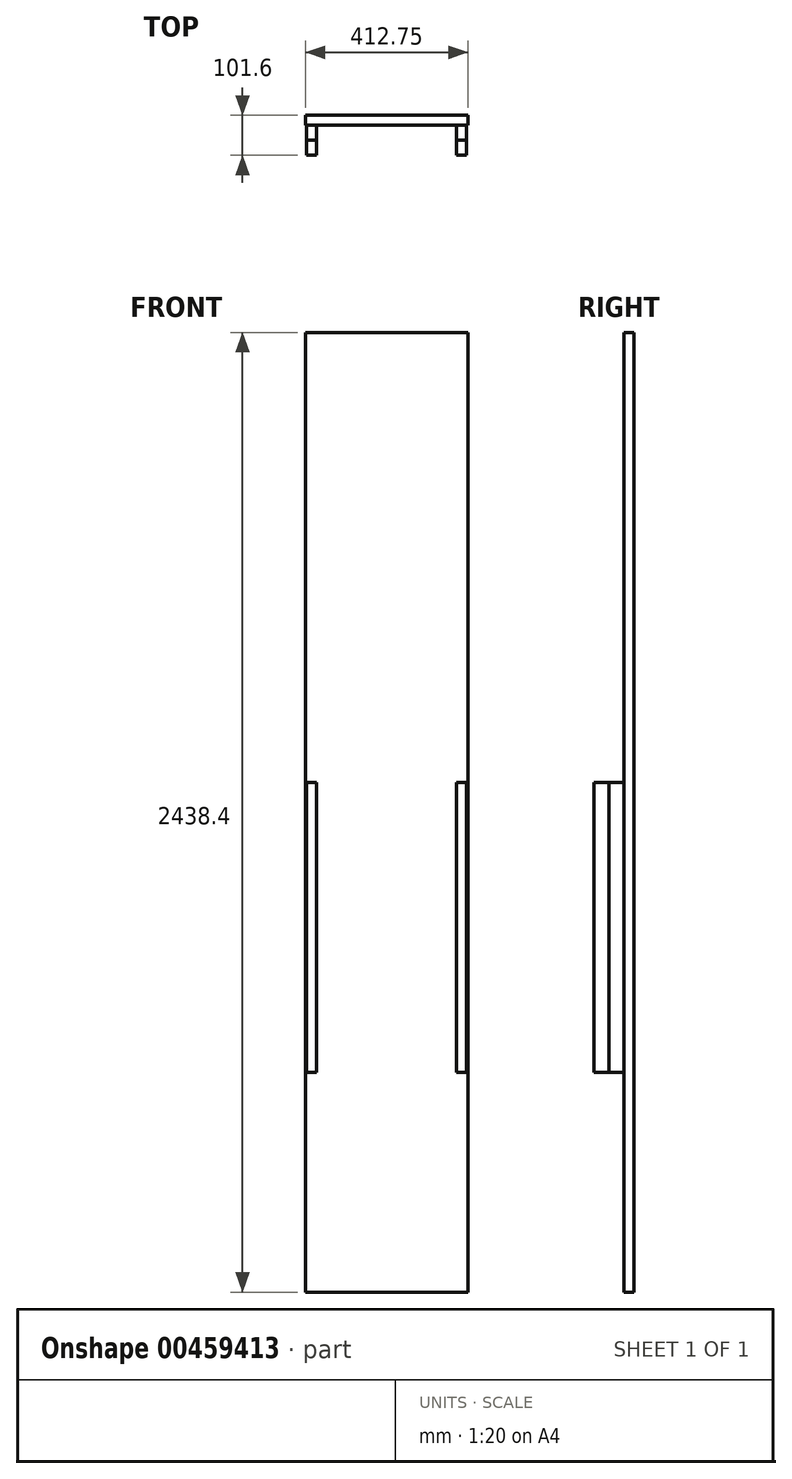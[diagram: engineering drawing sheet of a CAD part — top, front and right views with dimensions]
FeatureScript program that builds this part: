
annotation { "Feature Type Name" : "Feature", "Feature Type Description" : "" }
export const myFeature = defineFeature(function(context is Context, id is Id, definition is map)
    precondition{}
    {
        {
            var Q0;
            Q0=qCreatedBy(makeId("Front.planeOp"),FACE);
            var sketch = newSketch(context, id + "F0", { "sketchPlane" : qUnion([Q0])});
            skLineSegment(sketch, "E0.bottom", {"start": v(0, 0) * mm, "end": v(412.75, 0) * mm});
            skLineSegment(sketch, "E0.top", {"start": v(0, 2438.4) * mm, "end": v(412.75, 2438.4) * mm});
            skLineSegment(sketch, "E0.left", {"start": v(0, 0) * mm, "end": v(0, 2438.4) * mm});
            skLineSegment(sketch, "E0.right", {"start": v(412.75, 0) * mm, "end": v(412.75, 2438.4) * mm});
            skSolve(sketch);
        }
        {
            var Q0;
            Q0 = qSketchRegion(id + "F0", true);
            extrude(context, id + "F1", {"entities" : qUnion([Q0]), "depth" : 25.4 * mm});
        }
        {
            var Q0;
            Q0=makeQuery(id+"F1.opExtrude","CAP_FACE",FACE,{"disambiguationData":[OSD([sQuery(id+"F0.wireOp",EDGE,"E0.bottom"),sQuery(id+"F0.wireOp",EDGE,"E0.top"),sQuery(id+"F0.wireOp",EDGE,"E0.left"),sQuery(id+"F0.wireOp",EDGE,"E0.right")])],"isStart":false});
            var sketch = newSketch(context, id + "F2", { "sketchPlane" : qUnion([Q0])});
            skLineSegment(sketch, "E1.bottom", {"start": v(3.17, 863.6) * mm, "end": v(409.58, 863.6) * mm});
            skLineSegment(sketch, "E1.top", {"start": v(3.18, 127) * mm, "end": v(409.57, 127) * mm, "construction": true});
            skLineSegment(sketch, "E1.left", {"start": v(3.18, 863.6) * mm, "end": v(3.17, 127) * mm});
            skLineSegment(sketch, "E1.right", {"start": v(409.58, 863.6) * mm, "end": v(409.58, 127) * mm});
            skLineSegment(sketch, "E2", {"start": v(206.38, 127) * mm, "end": v(206.38, 0) * mm, "construction": true});
            skLineSegment(sketch, "E3", {"start": v(3.18, 127) * mm, "end": v(28.58, 127) * mm});
            skLineSegment(sketch, "E4", {"start": v(28.58, 127) * mm, "end": v(28.58, 800.1) * mm});
            skLineSegment(sketch, "E5", {"start": v(28.58, 800.1) * mm, "end": v(384.18, 800.1) * mm});
            skLineSegment(sketch, "E6", {"start": v(384.18, 800.1) * mm, "end": v(384.18, 127) * mm});
            skLineSegment(sketch, "E7", {"start": v(384.18, 127) * mm, "end": v(409.58, 127) * mm});
            skSolve(sketch);
        }
        {
            var Q0;
            Q0 = qSketchRegion(id + "F2", true);
            extrude(context, id + "F3", {"entities" : qUnion([Q0]), "depth" : 76.2 * mm});
        }
        {
            var Q0;
            Q0=makeQuery(id+"F1.opExtrude","CAP_FACE",FACE,{"disambiguationData":[OSD([sQuery(id+"F0.wireOp",EDGE,"E0.bottom"),sQuery(id+"F0.wireOp",EDGE,"E0.top"),sQuery(id+"F0.wireOp",EDGE,"E0.left"),sQuery(id+"F0.wireOp",EDGE,"E0.right")])],"isStart":false});
            var sketch = newSketch(context, id + "F4", { "sketchPlane" : qUnion([Q0])});
            skLineSegment(sketch, "E8.bottom", {"start": v(3.18, 711.2) * mm, "end": v(409.57, 711.2) * mm});
            skLineSegment(sketch, "E8.top", {"start": v(3.17, 1295.4) * mm, "end": v(409.58, 1295.4) * mm});
            skLineSegment(sketch, "E8.left", {"start": v(3.17, 711.2) * mm, "end": v(3.17, 1295.4) * mm});
            skLineSegment(sketch, "E8.right", {"start": v(409.58, 711.2) * mm, "end": v(409.57, 1295.4) * mm});
            skLineSegment(sketch, "E9", {"start": v(206.37, 711.2) * mm, "end": v(206.38, 0) * mm, "construction": true});
            skSolve(sketch);
        }
        {
            var Q0;
            Q0 = qSketchRegion(id + "F4", true);
            extrude(context, id + "F5", {"entities" : qUnion([Q0]), "depth" : 38.1 * mm});
        }
        {
            var Q0;
            Q0=makeQuery(id+"F5.opExtrude","CAP_FACE",FACE,{"disambiguationData":[OSD([sQuery(id+"F4.wireOp",EDGE,"E8.bottom"),sQuery(id+"F4.wireOp",EDGE,"E8.top"),sQuery(id+"F4.wireOp",EDGE,"E8.left"),sQuery(id+"F4.wireOp",EDGE,"E8.right")])],"isStart":false});
            var sketch = newSketch(context, id + "F6", { "sketchPlane" : qUnion([Q0])});
            skLineSegment(sketch, "E10", {"start": v(152.7, 1295.4) * mm, "end": v(148.35, 717.4) * mm});
            skSolve(sketch);
        }
        {
            var Q0;
            Q0=makeQuery(id+"F6.imprint","IMPRINT",FACE,{"disambiguationData":[TD([[makeQuery(id+"F6.imprint","IMPRINT",EDGE,{"derivedFrom":makeQuery(id+"F5.opExtrude","CAP_EDGE",EDGE,{"disambiguationData":[OSD([sQuery(id+"F4.wireOp",EDGE,"E8.bottom")])],"isStart":false})}),1.0]])]});
            var sketch = newSketch(context, id + "F7", { "sketchPlane" : qUnion([Q0])});
            skLineSegment(sketch, "E11.bottom", {"start": v(28.57, 1295.4) * mm, "end": v(3.17, 1295.4) * mm});
            skLineSegment(sketch, "E11.top", {"start": v(28.58, 558.8) * mm, "end": v(3.18, 558.8) * mm});
            skLineSegment(sketch, "E11.left", {"start": v(28.57, 1295.4) * mm, "end": v(28.58, 558.8) * mm});
            skLineSegment(sketch, "E11.right", {"start": v(3.17, 1295.4) * mm, "end": v(3.18, 558.8) * mm});
            skLineSegment(sketch, "E12.bottom", {"start": v(409.58, 558.8) * mm, "end": v(384.18, 558.8) * mm});
            skLineSegment(sketch, "E12.top", {"start": v(409.57, 1295.4) * mm, "end": v(384.17, 1295.4) * mm});
            skLineSegment(sketch, "E12.left", {"start": v(409.58, 558.8) * mm, "end": v(409.57, 1295.4) * mm});
            skLineSegment(sketch, "E12.right", {"start": v(384.18, 558.8) * mm, "end": v(384.17, 1295.4) * mm});
            skSolve(sketch);
        }
        {
            var Q0;
            Q0 = qSketchRegion(id + "F7", true);
            extrude(context, id + "F8", {"entities" : qUnion([Q0]), "depth" : 38.1 * mm});
        }
        {
            var Q0;
            Q0=makeQuery(id+"F8.opExtrude","CAP_FACE",FACE,{"disambiguationData":[OSD([sQuery(id+"F7.wireOp",EDGE,"E11.bottom"),sQuery(id+"F7.wireOp",EDGE,"E11.top"),sQuery(id+"F7.wireOp",EDGE,"E11.left"),sQuery(id+"F7.wireOp",EDGE,"E11.right")])],"isStart":true});
            var sketch = newSketch(context, id + "F9", { "sketchPlane" : qUnion([Q0])});
            skLineSegment(sketch, "E13.0.0", {"start": v(-28.58, 558.8) * mm, "end": v(-28.57, 1295.4) * mm});
            skLineSegment(sketch, "E13.0.1", {"start": v(-28.57, 1295.4) * mm, "end": v(-3.17, 1295.4) * mm});
            skLineSegment(sketch, "E13.0.2", {"start": v(-3.17, 1295.4) * mm, "end": v(-3.18, 558.8) * mm});
            skLineSegment(sketch, "E13.0.3", {"start": v(-3.18, 558.8) * mm, "end": v(-28.58, 558.8) * mm});
            skLineSegment(sketch, "E13.1.0", {"start": v(-384.17, 1295.4) * mm, "end": v(-384.18, 558.8) * mm});
            skLineSegment(sketch, "E13.1.1", {"start": v(-384.18, 558.8) * mm, "end": v(-409.58, 558.8) * mm});
            skLineSegment(sketch, "E13.1.2", {"start": v(-409.58, 558.8) * mm, "end": v(-409.57, 1295.4) * mm});
            skLineSegment(sketch, "E13.1.3", {"start": v(-409.57, 1295.4) * mm, "end": v(-384.17, 1295.4) * mm});
            skSolve(sketch);
        }
        {
            var Q0;
            Q0 = qSketchRegion(id + "F9", true);
            extrude(context, id + "F10", {"entities" : qUnion([Q0]), "depth" : 38.1 * mm});
        }
        {
            var Q0;
            Q0=makeQuery(id+"F3.opExtrude","SWEPT_BODY",BODY,{"disambiguationData":[OSD([sQuery(id+"F2.wireOp",EDGE,"E1.bottom"),sQuery(id+"F2.wireOp",EDGE,"E1.left"),sQuery(id+"F2.wireOp",EDGE,"E1.right"),sQuery(id+"F2.wireOp",EDGE,"E3"),sQuery(id+"F2.wireOp",EDGE,"E4"),sQuery(id+"F2.wireOp",EDGE,"E5"),sQuery(id+"F2.wireOp",EDGE,"E6"),sQuery(id+"F2.wireOp",EDGE,"E7")])]});
            var Q1;
            Q1=makeQuery(id+"F5.opExtrude","SWEPT_BODY",BODY,{"disambiguationData":[OSD([sQuery(id+"F4.wireOp",EDGE,"E8.bottom"),sQuery(id+"F4.wireOp",EDGE,"E8.top"),sQuery(id+"F4.wireOp",EDGE,"E8.left"),sQuery(id+"F4.wireOp",EDGE,"E8.right")])]});
            deleteBodies(context, id + "F11", {"entities" : qUnion([Q0, Q1])});
        }
    });
